# Revit family: Electrical_Equipment-Floor_Box-Hubbell_Wiring-AFBS1R4
name_source: partatom
category: Electrical Fixtures
revit_build: Autodesk Revit 2015 (Build: 20140606_1530(x64)
units: mm (PartAtom-declared; Revit-internal decimal feet)

## types (1)
- AFBS1R4
    Assembly Code = D5020115
    Conduit Connector_1 Description = 1 in, 0.75 in & 0.5 in Data Connection
    Conduit Connector_2 Description = 0.5 in. Data Connection
    Conduit Connector_3 Description = 0.5 in. Data Connection
    Conduit Connector_4 Description = 0.5 in. Data Connection
    Conduit Connector_5 Description = 0.5 in. Data Connection
    Default Elevation = 48 "
    Description = Raised Access Floor Box
    Manufacturer = Hubbell Wiring Device-Kellems
    Manufacturer Fax = 203-882-4852
    Model = AFBS1R4
    Product Documentation Link = http://www.hubbell-wiring.com
    Product Material = Metal-Hubbell-Galvanized_Steel
    Product Page URL = http://www.hubbell-wiring.com
    Product data url = https://bimobject.com
    URL = http://www.hubbell-wiring.com

## geometry (parser evidence)
native form markers: Blend x11, Sweep x4
no freeform markers — native parametric forms only
